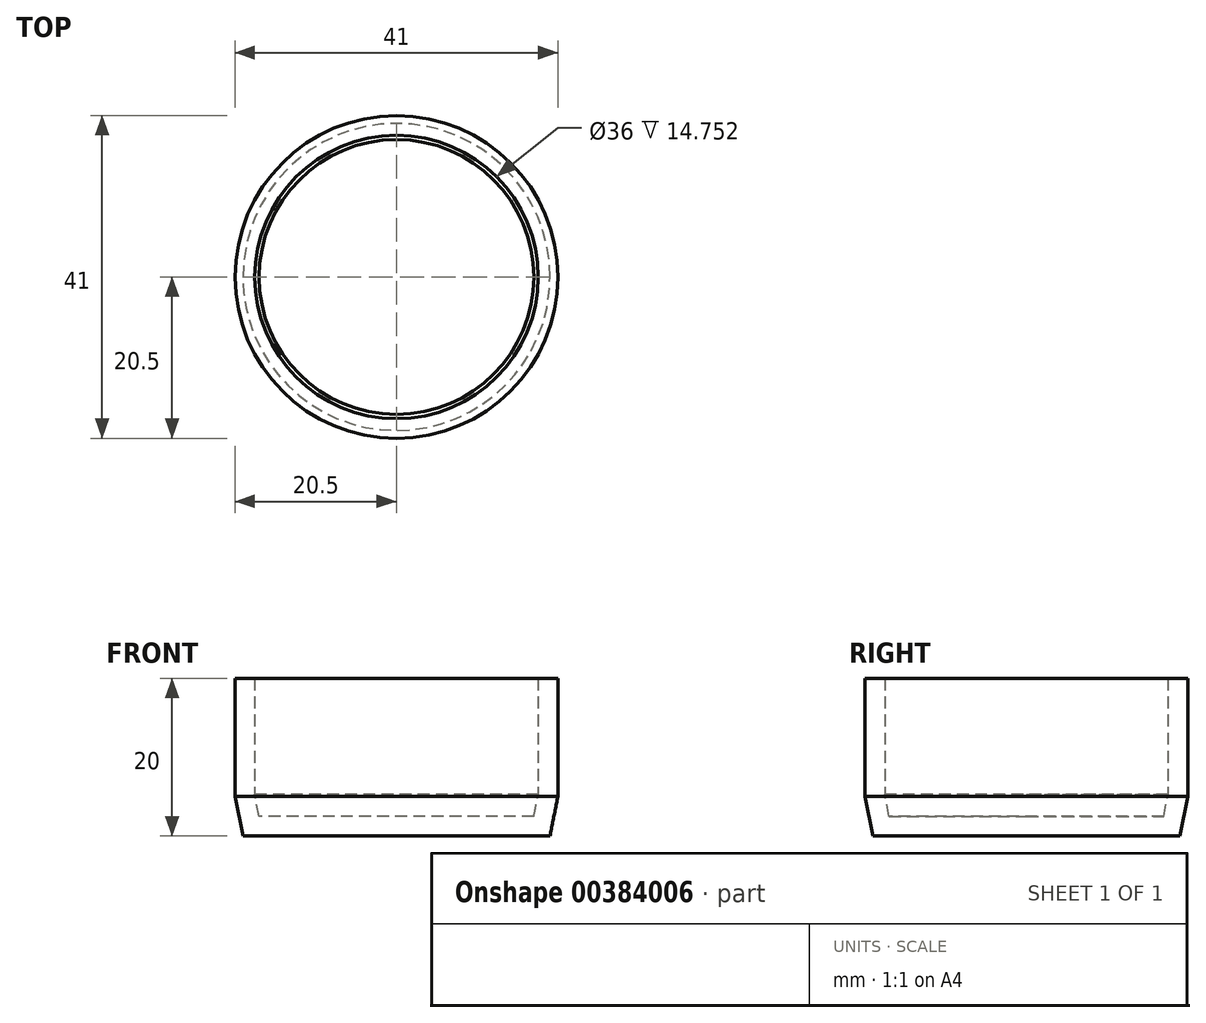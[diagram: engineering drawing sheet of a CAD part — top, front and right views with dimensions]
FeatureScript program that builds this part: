
annotation { "Feature Type Name" : "Feature", "Feature Type Description" : "" }
export const myFeature = defineFeature(function(context is Context, id is Id, definition is map)
    precondition{}
    {
        {
            var Q0;
            Q0=qCreatedBy(makeId("Top.planeOp"),FACE);
            var sketch = newSketch(context, id + "F0", { "sketchPlane" : qUnion([Q0])});
            skCircle(sketch, "E0", {"center": v(0, 0) * mm, "radius": 20.5 * mm});
            skSolve(sketch);
        }
        {
            var Q0;
            Q0 = qSketchRegion(id + "F0", true);
            extrude(context, id + "F1", {"entities" : qUnion([Q0]), "depth" : 20 * mm});
        }
        {
            var Q0;
            Q0=makeQuery(id+"F1.opExtrude","CAP_FACE",FACE,{"disambiguationData":[OSD([sQuery(id+"F0.wireOp",EDGE,"E0")])],"isStart":true});
            chamfer(context, id + "F2", {"entities" : qUnion([Q0]), "chamferType" : ChamferType.TWO_OFFSETS, "width1" : 5 * mm, "oppositeDirection" : false, "width2" : 1 * mm, "tangentPropagation" : true});
        }
        {
            var Q0;
            Q0=makeQuery(id+"F1.opExtrude","CAP_FACE",FACE,{"disambiguationData":[OSD([sQuery(id+"F0.wireOp",EDGE,"E0")])],"isStart":false});
            shell(context, id + "F3", {"entities" : qUnion([Q0]), "thickness" : 2.5 * mm});
        }
    });
